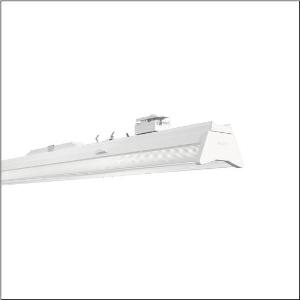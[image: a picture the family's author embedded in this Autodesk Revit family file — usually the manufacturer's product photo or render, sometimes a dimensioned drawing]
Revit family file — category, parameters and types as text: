
# Revit family: licross_r__11_performance_ho_51td16mn4gxm_b838
name_source: partatom
category: Lighting Fixtures
units: mm (PartAtom-declared; Revit-internal decimal feet)

## family parameters
Cut with Voids When Loaded = No
Host = Face
Light Source = No
Part Type = Normal
Room Calculation Point = No
Round Connector Dimension = Use Diameter
Shared = No

## types (1)
- --- (1 x LED, 16020 lm, 87.4 W, 4000K)
    Apparent Load = 87 VA
    CIE Flux Codes = 63 87 95 78 100
    Color Rendering = 80
    Color Temperature = 4000K
    Default Elevation = 1800 mm
    Description = Licross® 11 Performance HO, luminaire insert, of sheet steel, galvanised, coil coated, white, length: 1.500mm, width: 120mm, height: 123mm, LED rated luminous flux: 16.020lm, light colour: 840, control gear: ON/OFF Multilumen, with plug, 3-pole, with phase selection, mains connection: 220..240V, AC, 50/60Hz, rated input power: 87W, halogen-free wiring, primary light control with lens, of plastic, primary optical cover: cover, of PMMA, light emission: direct/indirect distribution, primary light characteristic: symmetric, protection rating (complete): IP54, insulation class (complete): insulation class I (protective earthing), certification: CE, ENEC, VDE, UKCA, protection symbol: D if used in an environment with non-conductive dust loads with corresponding accessories, impact resistance: IK06, permissible ambient temperature for indoor applications: -35..+35°C, corresponds to IFS (International Featured Standards) requirements for safety and quality in the food industry, reducing of maximum allowable ambient temperature of 5°C with ceiling mounting, LABS conformity tested according to VDMA 24364:2018-05, packaging unit: 1 piece
    Height = 114 mm
    Lamp = 1 x LED
    Lamp Light Flux = 16020 lm
    Lamp Power = 87.4 W
    Lamp count = 1
    Length = 1500 mm
    Luminous efficacy = 183 lm/W
    Manufacturer = Siteco
    ModVariant = No
    Model = 51TD16MN4GXM
    Mounting Place = Ceiling
    Mounting Type = Pendant
    Number of Poles = 1
    OnlyDefault = Yes
    Power Factor = 1
    Product Name = Licross® 11 Performance HO
    Product group = luminaire insert
    ProductGroupID = 901
    Protection Class = Protection class I
    Protection Degree = IP 54
    RLX_Detail_Level = 1
    RLX_Emergency_Light_Flux = 0 lm
    RLX_Emergency_Type = 0
    RLX_Emergency_Type_DB = No
    RlxData = <blob elided: 31749 chars, md5=fde10fdb>
    Socket = socket
    Standby Power = 0 W
    System Light Flux = 16020 lm
    System Power = 87 W
    Type Comments = factory setting: luminous flux: 100 % | (A | C | E) | 203 mA
    Type Image = l_1256138.jpg
    URL = http://relux.com
    VarID = @adj_055533
    Voltage = 0 V
    Weight = 0.00 kg
    Width = 120 mm

## geometry (parser evidence)
native form markers: Blend x4, Sweep x12
no freeform markers — native parametric forms only
